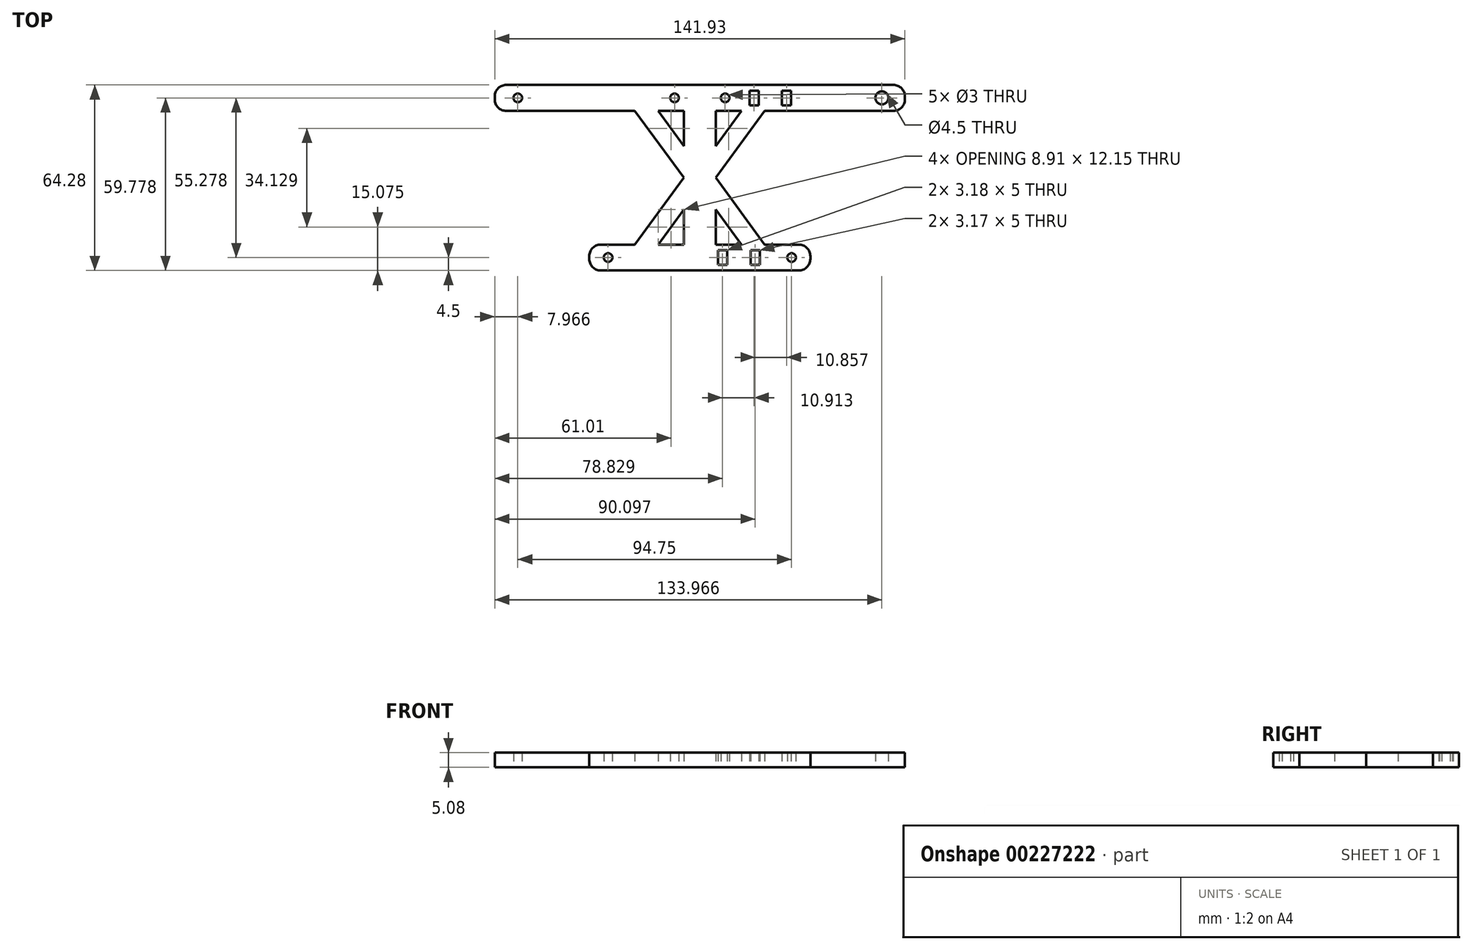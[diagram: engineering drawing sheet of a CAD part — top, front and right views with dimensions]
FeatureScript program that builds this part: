
annotation { "Feature Type Name" : "Feature", "Feature Type Description" : "" }
export const myFeature = defineFeature(function(context is Context, id is Id, definition is map)
    precondition{}
    {
        {
            var Q0;
            Q0=qCreatedBy(makeId("Top.planeOp"),FACE);
            var sketch = newSketch(context, id + "F0", { "sketchPlane" : qUnion([Q0])});
            skCircle(sketch, "E0", {"center": v(-52.08, 55.28) * mm, "radius": 1.5 * mm});
            skCircle(sketch, "E1", {"center": v(-20.83, 0) * mm, "radius": 1.5 * mm});
            skLineSegment(sketch, "E2", {"start": v(-20.83, 0) * mm, "end": v(10.92, 0) * mm});
            skLineSegment(sketch, "E3", {"start": v(-20.83, 0) * mm, "end": v(-52.08, 55.28) * mm});
            skLineSegment(sketch, "E4", {"start": v(-52.08, 55.28) * mm, "end": v(10.92, 55.28) * mm});
            skPoint(sketch, "E5.middle", {"position": v(10.92, 55.28) * mm});
            skPoint(sketch, "E6.middle", {"position": v(10.92, 0) * mm});
            skLineSegment(sketch, "E7", {"start": v(10.92, 0) * mm, "end": v(10.92, 55.28) * mm});
            skPoint(sketch, "E8.middle", {"position": v(10.92, 27.64) * mm});
            skLineSegment(sketch, "E9.MirrorCS", {"start": v(73.92, 55.28) * mm, "end": v(10.92, 55.28) * mm});
            skLineSegment(sketch, "E10.MirrorCS", {"start": v(42.67, 0) * mm, "end": v(73.92, 55.28) * mm});
            skLineSegment(sketch, "E11.MirrorCS", {"start": v(42.67, 0) * mm, "end": v(10.92, 0) * mm});
            skCircle(sketch, "E12.MirrorC", {"center": v(42.67, 0) * mm, "radius": 1.5 * mm});
            skPoint(sketch, "E13.middle", {"position": v(73.92, 55.28) * mm});
            skCircle(sketch, "E14", {"center": v(73.92, 55.28) * mm, "radius": 2.25 * mm});
            skLineSegment(sketch, "E15.bottom", {"start": v(81.88, 59.78) * mm, "end": v(-60.05, 59.78) * mm});
            skLineSegment(sketch, "E15.top", {"start": v(81.88, 50.78) * mm, "end": v(-60.05, 50.78) * mm});
            skLineSegment(sketch, "E15.left", {"start": v(81.88, 59.78) * mm, "end": v(81.88, 50.78) * mm});
            skLineSegment(sketch, "E15.right", {"start": v(-60.05, 59.78) * mm, "end": v(-60.05, 50.78) * mm});
            skLineSegment(sketch, "E16.bottom", {"start": v(49.17, 4.5) * mm, "end": v(-27.34, 4.5) * mm});
            skLineSegment(sketch, "E16.top", {"start": v(49.17, -4.5) * mm, "end": v(-27.34, -4.5) * mm});
            skLineSegment(sketch, "E16.left", {"start": v(49.17, 4.5) * mm, "end": v(49.17, -4.5) * mm});
            skLineSegment(sketch, "E16.right", {"start": v(-27.34, 4.5) * mm, "end": v(-27.34, -4.5) * mm});
            skLineSegment(sketch, "E17", {"start": v(5.42, 50.78) * mm, "end": v(5.42, 4.5) * mm});
            skLineSegment(sketch, "E18.MirrorCS", {"start": v(16.42, 50.78) * mm, "end": v(16.42, 4.5) * mm});
            skLineSegment(sketch, "E19", {"start": v(5.42, 27.64) * mm, "end": v(16.42, 27.64) * mm});
            skLineSegment(sketch, "E20", {"start": v(-11.56, 50.78) * mm, "end": v(5.42, 27.64) * mm});
            skLineSegment(sketch, "E21", {"start": v(-3.5, 50.78) * mm, "end": v(5.42, 38.63) * mm});
            skLineSegment(sketch, "E22.MirrorCS", {"start": v(25.33, 50.78) * mm, "end": v(16.42, 38.63) * mm});
            skLineSegment(sketch, "E23.MirrorCS", {"start": v(33.39, 50.78) * mm, "end": v(16.42, 27.64) * mm});
            skLineSegment(sketch, "E24.MirrorCS", {"start": v(33.39, 4.5) * mm, "end": v(16.42, 27.64) * mm});
            skLineSegment(sketch, "E25.MirrorCS", {"start": v(25.33, 4.5) * mm, "end": v(16.42, 16.65) * mm});
            skLineSegment(sketch, "E26.MirrorCS", {"start": v(-3.5, 4.5) * mm, "end": v(5.42, 16.65) * mm});
            skLineSegment(sketch, "E27.MirrorCS", {"start": v(-11.56, 4.5) * mm, "end": v(5.42, 27.64) * mm});
            skLineSegment(sketch, "E28.bottom", {"start": v(31.63, 2.5) * mm, "end": v(28.46, 2.5) * mm});
            skLineSegment(sketch, "E28.top", {"start": v(31.63, -2.5) * mm, "end": v(28.46, -2.5) * mm});
            skLineSegment(sketch, "E28.left", {"start": v(31.63, 2.5) * mm, "end": v(31.63, -2.5) * mm});
            skLineSegment(sketch, "E28.right", {"start": v(28.46, 2.5) * mm, "end": v(28.46, -2.5) * mm});
            skPoint(sketch, "E28.middle", {"position": v(30.05, 0) * mm});
            skCircle(sketch, "E29", {"center": v(19.67, 55.28) * mm, "radius": 1.5 * mm});
            skCircle(sketch, "E30.MirrorC", {"center": v(2.17, 55.28) * mm, "radius": 1.5 * mm});
            skLineSegment(sketch, "E31.bottom", {"start": v(20.37, 2.5) * mm, "end": v(17.2, 2.5) * mm});
            skLineSegment(sketch, "E31.top", {"start": v(20.37, -2.5) * mm, "end": v(17.2, -2.5) * mm});
            skLineSegment(sketch, "E31.left", {"start": v(20.37, 2.5) * mm, "end": v(20.37, -2.5) * mm});
            skLineSegment(sketch, "E31.right", {"start": v(17.2, 2.5) * mm, "end": v(17.2, -2.5) * mm});
            skLineSegment(sketch, "E32", {"start": v(28.1, 57.74) * mm, "end": v(28.1, 52.74) * mm});
            skLineSegment(sketch, "E33", {"start": v(28.1, 52.74) * mm, "end": v(31.28, 52.74) * mm});
            skLineSegment(sketch, "E34", {"start": v(31.28, 52.74) * mm, "end": v(31.28, 57.74) * mm});
            skLineSegment(sketch, "E35", {"start": v(31.28, 57.74) * mm, "end": v(28.1, 57.74) * mm});
            skLineSegment(sketch, "E36.bottom", {"start": v(39.32, 57.74) * mm, "end": v(42.5, 57.74) * mm});
            skLineSegment(sketch, "E36.top", {"start": v(39.32, 52.74) * mm, "end": v(42.5, 52.74) * mm});
            skLineSegment(sketch, "E36.left", {"start": v(39.32, 57.74) * mm, "end": v(39.32, 52.74) * mm});
            skLineSegment(sketch, "E36.right", {"start": v(42.5, 57.74) * mm, "end": v(42.5, 52.74) * mm});
            skSolve(sketch);
        }
        {
            var Q0;
            {var subQ5=sQuery(id+"F0.wireOp",EDGE,"E0");var subQ7=sQuery(id+"F0.wireOp",EDGE,"E3");var subQ8=makeQuery(id+"F0.imprint","INTERSECT",VERTEX,{"derivedFrom":[subQ5,subQ7]});Q0=makeQuery(id+"F0.imprint","IMPRINT",FACE,{"disambiguationData":[TD([[makeQuery(id+"F0.imprint","IMPRINT",EDGE,{"disambiguationData":[TD([[subQ8,-1.0]])],"derivedFrom":subQ5}),-1.0]])]});}
            var Q1;
            {var subQ1=sQuery(id+"F0.wireOp",EDGE,"E2");var subQ5=sQuery(id+"F0.wireOp",EDGE,"E1");var subQ6=makeQuery(id+"F0.imprint","INTERSECT",VERTEX,{"derivedFrom":[subQ5,subQ1]});Q1=makeQuery(id+"F0.imprint","IMPRINT",FACE,{"disambiguationData":[TD([[makeQuery(id+"F0.imprint","IMPRINT",EDGE,{"disambiguationData":[TD([[subQ6,-1.0]])],"derivedFrom":subQ5}),-1.0]])]});}
            var Q2;
            Q2=makeQuery(id+"F0.imprint","IMPRINT",FACE,{"disambiguationData":[TD([[makeQuery(id+"F0.imprint","IMPRINT",EDGE,{"derivedFrom":sQuery(id+"F0.wireOp",EDGE,"E15.bottom")}),1.0]])]});
            var Q3;
            Q3=makeQuery(id+"F0.imprint","IMPRINT",FACE,{"disambiguationData":[TD([[makeQuery(id+"F0.imprint","IMPRINT",EDGE,{"derivedFrom":sQuery(id+"F0.wireOp",EDGE,"E16.top")}),-1.0]])]});
            var Q4;
            {var subQ1=sQuery(id+"F0.wireOp",EDGE,"E10.MirrorCS");var subQ5=sQuery(id+"F0.wireOp",EDGE,"E16.bottom");var subQ6=makeQuery(id+"F0.imprint","INTERSECT",VERTEX,{"derivedFrom":[subQ1,subQ5]});Q4=makeQuery(id+"F0.imprint","IMPRINT",FACE,{"disambiguationData":[TD([[makeQuery(id+"F0.imprint","IMPRINT",EDGE,{"disambiguationData":[TD([[subQ6,1.0]])],"derivedFrom":subQ1}),1.0]])]});}
            var Q5;
            {var subQ0=sQuery(id+"F0.wireOp",EDGE,"E15.top");var subQ1=sQuery(id+"F0.wireOp",EDGE,"E10.MirrorCS");var subQ2=makeQuery(id+"F0.imprint","INTERSECT",VERTEX,{"derivedFrom":[subQ1,subQ0]});Q5=makeQuery(id+"F0.imprint","IMPRINT",FACE,{"disambiguationData":[TD([[makeQuery(id+"F0.imprint","IMPRINT",EDGE,{"disambiguationData":[TD([[subQ2,-1.0]])],"derivedFrom":subQ1}),1.0]])]});}
            var Q6;
            {var subQ5=sQuery(id+"F0.wireOp",EDGE,"E17");Q6=makeQuery(id+"F0.imprint","IMPRINT",FACE,{"disambiguationData":[TD([[makeQuery(id+"F0.imprint","IMPRINT",EDGE,{"derivedFrom":subQ5}),1.0]])]});}
            var Q7;
            {var subQ5=sQuery(id+"F0.wireOp",EDGE,"E18.MirrorCS");Q7=makeQuery(id+"F0.imprint","IMPRINT",FACE,{"disambiguationData":[TD([[makeQuery(id+"F0.imprint","IMPRINT",EDGE,{"derivedFrom":subQ5}),-1.0]])]});}
            var Q8;
            {var subQ0=sQuery(id+"F0.wireOp",EDGE,"feb966cf-f615-44a7-a13d-1bd144c4b3750.MirrorCS");Q8=makeQuery(id+"F0.imprint","IMPRINT",FACE,{"disambiguationData":[TD([[makeQuery(id+"F0.imprint","IMPRINT",EDGE,{"derivedFrom":subQ0}),-1.0]])]});}
            var Q9;
            {var subQ0=sQuery(id+"F0.wireOp",EDGE,"d3fe900e-5d7e-4329-a638-1e34b492a3660.MirrorCS");Q9=makeQuery(id+"F0.imprint","IMPRINT",FACE,{"disambiguationData":[TD([[makeQuery(id+"F0.imprint","IMPRINT",EDGE,{"derivedFrom":subQ0}),1.0]])]});}
            var Q10;
            {var subQ0=sQuery(id+"F0.wireOp",EDGE,"hfX9tZ72-0kb9-5i1I-bADh-dzFUvOyJdu75");Q10=makeQuery(id+"F0.imprint","IMPRINT",FACE,{"disambiguationData":[TD([[makeQuery(id+"F0.imprint","IMPRINT",EDGE,{"derivedFrom":subQ0}),-1.0]])]});}
            var Q11;
            {var subQ0=sQuery(id+"F0.wireOp",EDGE,"7ac03fb2-961d-4cd1-b936-0828aa2fb5720.MirrorCS");Q11=makeQuery(id+"F0.imprint","IMPRINT",FACE,{"disambiguationData":[TD([[makeQuery(id+"F0.imprint","IMPRINT",EDGE,{"derivedFrom":subQ0}),-1.0]])]});}
            var Q12;
            {var subQ0=sQuery(id+"F0.wireOp",EDGE,"E20");Q12=makeQuery(id+"F0.imprint","IMPRINT",FACE,{"disambiguationData":[TD([[makeQuery(id+"F0.imprint","IMPRINT",EDGE,{"derivedFrom":subQ0}),1.0]])]});}
            var Q13;
            {var subQ0=sQuery(id+"F0.wireOp",EDGE,"E26.MirrorCS");Q13=makeQuery(id+"F0.imprint","IMPRINT",FACE,{"disambiguationData":[TD([[makeQuery(id+"F0.imprint","IMPRINT",EDGE,{"derivedFrom":subQ0}),1.0]])]});}
            var Q14;
            {var subQ0=sQuery(id+"F0.wireOp",EDGE,"E24.MirrorCS");Q14=makeQuery(id+"F0.imprint","IMPRINT",FACE,{"disambiguationData":[TD([[makeQuery(id+"F0.imprint","IMPRINT",EDGE,{"derivedFrom":subQ0}),1.0]])]});}
            var Q15;
            {var subQ0=sQuery(id+"F0.wireOp",EDGE,"E22.MirrorCS");Q15=makeQuery(id+"F0.imprint","IMPRINT",FACE,{"disambiguationData":[TD([[makeQuery(id+"F0.imprint","IMPRINT",EDGE,{"derivedFrom":subQ0}),1.0]])]});}
            extrude(context, id + "F1", {"entities" : qUnion([Q0, Q1, Q2, Q3, Q4, Q5, Q6, Q7, Q8, Q9, Q10, Q11, Q12, Q13, Q14, Q15]), "depth" : 5.08 * mm});
        }
        {
            var Q0;
            Q0=makeQuery(id+"F1.opExtrude","SWEPT_EDGE",EDGE,{"disambiguationData":[OSD([sQuery(id+"F0.wireOp",EDGE,"E15.bottom"),sQuery(id+"F0.wireOp",EDGE,"E15.right")])]});
            var Q1;
            Q1=makeQuery(id+"F1.opExtrude","SWEPT_EDGE",EDGE,{"disambiguationData":[OSD([sQuery(id+"F0.wireOp",EDGE,"E15.top"),sQuery(id+"F0.wireOp",EDGE,"E15.right")])]});
            var Q2;
            Q2=makeQuery(id+"F1.opExtrude","SWEPT_EDGE",EDGE,{"disambiguationData":[OSD([sQuery(id+"F0.wireOp",EDGE,"E15.bottom"),sQuery(id+"F0.wireOp",EDGE,"E15.left")])]});
            var Q3;
            Q3=makeQuery(id+"F1.opExtrude","SWEPT_EDGE",EDGE,{"disambiguationData":[OSD([sQuery(id+"F0.wireOp",EDGE,"E15.top"),sQuery(id+"F0.wireOp",EDGE,"E15.left")])]});
            var Q4;
            Q4=makeQuery(id+"F1.opExtrude","SWEPT_EDGE",EDGE,{"disambiguationData":[OSD([sQuery(id+"F0.wireOp",EDGE,"E16.bottom"),sQuery(id+"F0.wireOp",EDGE,"E16.left")])]});
            var Q5;
            Q5=makeQuery(id+"F1.opExtrude","SWEPT_EDGE",EDGE,{"disambiguationData":[OSD([sQuery(id+"F0.wireOp",EDGE,"E16.top"),sQuery(id+"F0.wireOp",EDGE,"E16.left")])]});
            var Q6;
            Q6=makeQuery(id+"F1.opExtrude","SWEPT_EDGE",EDGE,{"disambiguationData":[OSD([sQuery(id+"F0.wireOp",EDGE,"E16.bottom"),sQuery(id+"F0.wireOp",EDGE,"E16.right")])]});
            var Q7;
            Q7=makeQuery(id+"F1.opExtrude","SWEPT_EDGE",EDGE,{"disambiguationData":[OSD([sQuery(id+"F0.wireOp",EDGE,"E16.top"),sQuery(id+"F0.wireOp",EDGE,"E16.right")])]});
            fillet(context, id + "F2", {"entities" : qUnion([Q0, Q1, Q2, Q3, Q4, Q5, Q6, Q7]), "radius" : 4 * mm, "tangentPropagation" : true, "allowEdgeOverflow" : false});
        }
    });
